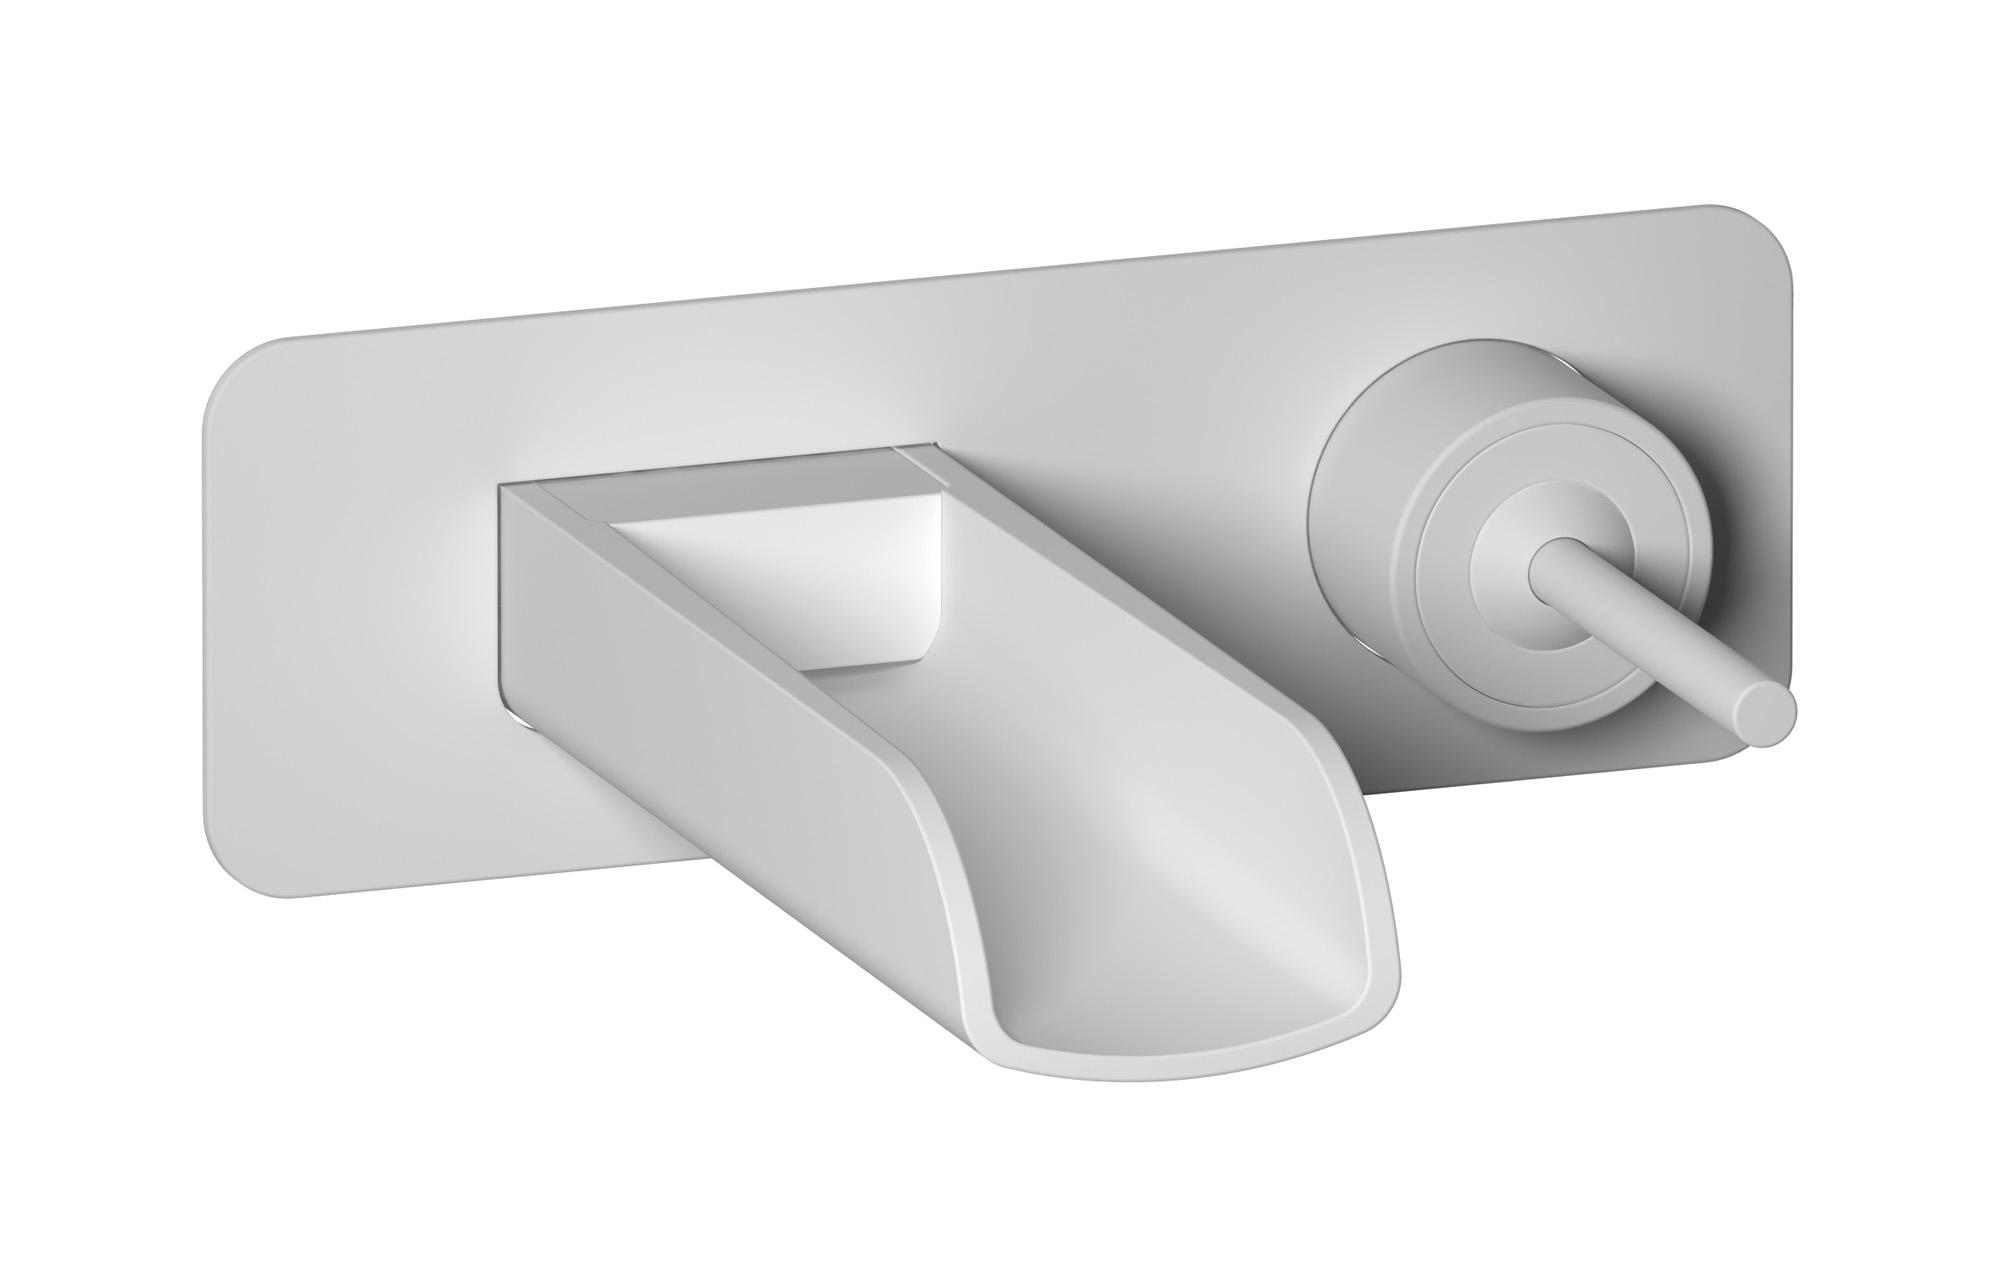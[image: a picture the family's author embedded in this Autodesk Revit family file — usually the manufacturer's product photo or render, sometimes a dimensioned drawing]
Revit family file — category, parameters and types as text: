
# Revit family: LM207
name_source: partatom
category: Apparecchi idraulici
units: mm (PartAtom-declared; Revit-internal decimal feet)

## family parameters
Basato su piano di lavoro = No
Condiviso = No
Mantieni orientamento annotazione = No
Numero OmniClass = 23.45.55.17
Punto di calcolo locali = No
Quota connettore circolare = Usa diametro
Sempre verticale = Sì
Taglio con vuoti quando caricato = No
Tipo di parte = Normale
Titolo OmniClass = Mixing Faucets

## types (9) — shared parameters
Cold water inlet = 10 mm  [stored 0.0328084 ft]
Commenti sul tipo = Washbasin mixer
Connessione CW = No
Connessione HW = No
Connessione di scarico = No
Connessione di ventilazione = No
Descrizione = Wall mounted washbasin mixer with long spout complete with drain
Hot water inlet = 10 mm  [stored 0.0328084 ft]
Produttore = IB Rubinetterie S.p.A.
URL = https://www.weareib.it
zero-valued in all types: Prospetto di default

## per-type parameters (varying)
| type | Finishes surface | Immagine tipo | Modello |
| Chrome | IB_Chrome | LM207CC.jpg | LM207CC |
| Brushed nickel | IB_Brushed nickel | LM207SS.jpg | LM207SS |
| Matt white | IB_matt white | LM207BO.jpg | LM207BO |
| Matt black | IB_matt black | LM207NP.jpg | LM207NP |
| Natural brass | IB_Brass | LM207ON.jpg | LM207ON |
| Brushed black chrome | IB_Brushed black chrome | LM207CS.jpg | LM207CS |
| Brushed pale gold | IB_brushed pale gold | LM207IS.jpg | LM207IS |
| Brushed rose gold | IB_Brushed rose gold | LM207SR.jpg | LM207SR |
| Brushed gold | IB_brushed gold | LM207OS.jpg | LM207OS |

note: [stored X ft] marks values corroborated as IEEE doubles in the binary element streams (Revit-internal decimal feet)
